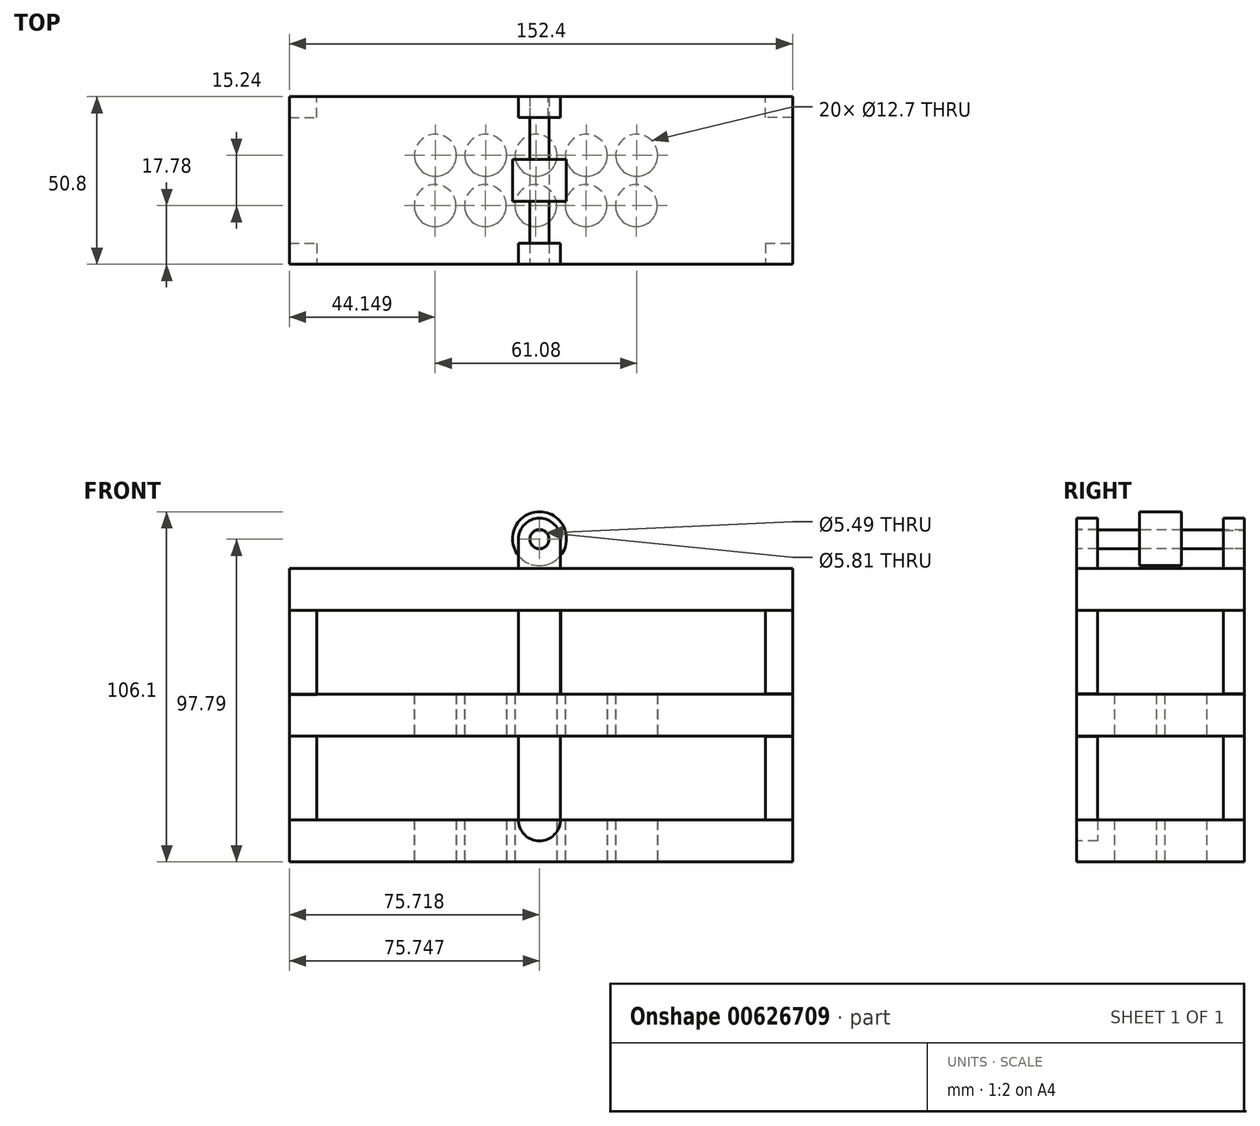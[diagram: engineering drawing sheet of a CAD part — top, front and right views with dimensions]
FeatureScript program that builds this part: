
annotation { "Feature Type Name" : "Feature", "Feature Type Description" : "" }
export const myFeature = defineFeature(function(context is Context, id is Id, definition is map)
    precondition{}
    {
        {
            var Q0;
            Q0=qCreatedBy(makeId("Front.planeOp"),FACE);
            var sketch = newSketch(context, id + "F0", { "sketchPlane" : qUnion([Q0])});
            skLineSegment(sketch, "E0", {"start": v(0, 88.9) * mm, "end": v(152.4, 88.9) * mm});
            skLineSegment(sketch, "E1", {"start": v(152.4, 0) * mm, "end": v(0, 0) * mm});
            skLineSegment(sketch, "E2", {"start": v(0, 0) * mm, "end": v(0, 12.7) * mm});
            skLineSegment(sketch, "E3", {"start": v(0, 12.7) * mm, "end": v(152.4, 12.7) * mm});
            skLineSegment(sketch, "E4", {"start": v(152.4, 12.7) * mm, "end": v(152.4, 0) * mm});
            skLineSegment(sketch, "E5", {"start": v(0, 38.1) * mm, "end": v(152.4, 38.1) * mm});
            skLineSegment(sketch, "E6", {"start": v(152.4, 38.1) * mm, "end": v(152.4, 50.8) * mm});
            skLineSegment(sketch, "E7", {"start": v(152.4, 50.8) * mm, "end": v(0, 50.8) * mm});
            skLineSegment(sketch, "E8", {"start": v(0, 50.8) * mm, "end": v(0, 38.1) * mm});
            skLineSegment(sketch, "E9", {"start": v(152.4, 88.9) * mm, "end": v(152.4, 76.2) * mm});
            skLineSegment(sketch, "E10", {"start": v(152.4, 76.2) * mm, "end": v(0, 76.2) * mm});
            skLineSegment(sketch, "E11", {"start": v(0, 76.2) * mm, "end": v(0, 88.9) * mm});
            skSolve(sketch);
        }
        {
            var Q0;
            Q0=makeQuery(id+"F0.imprint","IMPRINT",FACE,{"disambiguationData":[TD([[makeQuery(id+"F0.imprint","IMPRINT",EDGE,{"derivedFrom":sQuery(id+"F0.wireOp",EDGE,"E0")}),-1.0]])]});
            var Q1;
            Q1=makeQuery(id+"F0.imprint","IMPRINT",FACE,{"disambiguationData":[TD([[makeQuery(id+"F0.imprint","IMPRINT",EDGE,{"derivedFrom":sQuery(id+"F0.wireOp",EDGE,"E5")}),1.0]])]});
            var Q2;
            Q2=makeQuery(id+"F0.imprint","IMPRINT",FACE,{"disambiguationData":[TD([[makeQuery(id+"F0.imprint","IMPRINT",EDGE,{"derivedFrom":sQuery(id+"F0.wireOp",EDGE,"E1")}),-1.0]])]});
            extrude(context, id + "F1", {"entities" : qUnion([Q0, Q1, Q2]), "oppositeDirection" : true, "depth" : 50.8 * mm, "offsetDistance" : 25.4 * mm});
        }
        {
            var Q0;
            Q0=qCreatedBy(makeId("Front.planeOp"),FACE);
            var sketch = newSketch(context, id + "F2", { "sketchPlane" : qUnion([Q0])});
            skLineSegment(sketch, "E12", {"start": v(0, 12.76) * mm, "end": v(8.26, 12.76) * mm});
            skLineSegment(sketch, "E13", {"start": v(8.26, 12.76) * mm, "end": v(8.26, 38.1) * mm});
            skLineSegment(sketch, "E14", {"start": v(8.26, 38.1) * mm, "end": v(0, 38.1) * mm});
            skLineSegment(sketch, "E15", {"start": v(0, 38.1) * mm, "end": v(0, 12.76) * mm});
            skLineSegment(sketch, "E16", {"start": v(8.26, 50.75) * mm, "end": v(0, 50.75) * mm});
            skLineSegment(sketch, "E17", {"start": v(0, 50.75) * mm, "end": v(0, 76.24) * mm});
            skLineSegment(sketch, "E18", {"start": v(0, 76.24) * mm, "end": v(8.26, 76.24) * mm});
            skLineSegment(sketch, "E19", {"start": v(8.26, 76.24) * mm, "end": v(8.26, 50.75) * mm});
            skSolve(sketch);
        }
        {
            var Q0;
            Q0=makeQuery(id+"F1.opExtrude","CAP_FACE",FACE,{"disambiguationData":[OSD([sQuery(id+"F0.wireOp",EDGE,"E1"),sQuery(id+"F0.wireOp",EDGE,"E2"),sQuery(id+"F0.wireOp",EDGE,"E3"),sQuery(id+"F0.wireOp",EDGE,"E4")])],"isStart":true});
            var sketch = newSketch(context, id + "F3", { "sketchPlane" : qUnion([Q0])});
            skLineSegment(sketch, "E20", {"start": v(152.4, 12.7) * mm, "end": v(152.4, 37.95) * mm});
            skLineSegment(sketch, "E21", {"start": v(152.4, 37.95) * mm, "end": v(144.14, 37.95) * mm});
            skLineSegment(sketch, "E22", {"start": v(144.14, 37.95) * mm, "end": v(144.14, 12.7) * mm});
            skLineSegment(sketch, "E23", {"start": v(144.14, 12.7) * mm, "end": v(152.4, 12.7) * mm});
            skLineSegment(sketch, "E24", {"start": v(152.4, 50.88) * mm, "end": v(152.4, 76.21) * mm});
            skLineSegment(sketch, "E25", {"start": v(152.4, 76.21) * mm, "end": v(144.14, 76.21) * mm});
            skLineSegment(sketch, "E26", {"start": v(144.14, 76.21) * mm, "end": v(144.14, 50.88) * mm});
            skLineSegment(sketch, "E27", {"start": v(144.14, 50.88) * mm, "end": v(152.4, 50.88) * mm});
            skSolve(sketch);
        }
        {
            var Q0;
            Q0=makeQuery(id+"F3.imprint","IMPRINT",FACE,{"disambiguationData":[TD([[makeQuery(id+"F3.imprint","IMPRINT",EDGE,{"derivedFrom":sQuery(id+"F3.wireOp",EDGE,"E24")}),1.0]])]});
            var Q1;
            Q1=makeQuery(id+"F3.imprint","IMPRINT",FACE,{"disambiguationData":[TD([[makeQuery(id+"F3.imprint","IMPRINT",EDGE,{"derivedFrom":sQuery(id+"F3.wireOp",EDGE,"E20")}),1.0]])]});
            var Q2;
            Q2=makeQuery(id+"F2.imprint","IMPRINT",FACE,{"disambiguationData":[TD([[makeQuery(id+"F2.imprint","IMPRINT",EDGE,{"derivedFrom":sQuery(id+"F2.wireOp",EDGE,"E12")}),1.0]])]});
            var Q3;
            Q3=makeQuery(id+"F2.imprint","IMPRINT",FACE,{"disambiguationData":[TD([[makeQuery(id+"F2.imprint","IMPRINT",EDGE,{"derivedFrom":sQuery(id+"F2.wireOp",EDGE,"E16")}),-1.0]])]});
            extrude(context, id + "F4", {"entities" : qUnion([Q0, Q1, Q2, Q3]), "oppositeDirection" : true, "depth" : 6.35 * mm, "offsetDistance" : 25.4 * mm});
        }
        {
            var Q0;
            Q0=makeQuery(id+"F1.opExtrude","CAP_FACE",FACE,{"disambiguationData":[OSD([sQuery(id+"F0.wireOp",EDGE,"E1"),sQuery(id+"F0.wireOp",EDGE,"E2"),sQuery(id+"F0.wireOp",EDGE,"E3"),sQuery(id+"F0.wireOp",EDGE,"E4")])],"isStart":false});
            var sketch = newSketch(context, id + "F5", { "sketchPlane" : qUnion([Q0])});
            skLineSegment(sketch, "E28", {"start": v(-152.4, 12.7) * mm, "end": v(-152.4, 38.13) * mm});
            skLineSegment(sketch, "E29", {"start": v(-152.4, 38.13) * mm, "end": v(-144.14, 38.13) * mm});
            skLineSegment(sketch, "E30", {"start": v(-144.14, 38.13) * mm, "end": v(-144.14, 12.7) * mm});
            skLineSegment(sketch, "E31", {"start": v(-144.14, 12.7) * mm, "end": v(-152.4, 12.7) * mm});
            skLineSegment(sketch, "E32", {"start": v(-152.4, 50.94) * mm, "end": v(-144.14, 50.94) * mm});
            skLineSegment(sketch, "E33", {"start": v(-144.14, 50.94) * mm, "end": v(-144.14, 76.26) * mm});
            skLineSegment(sketch, "E34", {"start": v(-144.14, 76.26) * mm, "end": v(-152.4, 76.26) * mm});
            skLineSegment(sketch, "E35", {"start": v(-152.4, 76.26) * mm, "end": v(-152.4, 50.94) * mm});
            skLineSegment(sketch, "E36", {"start": v(0, 12.7) * mm, "end": v(0, 38.13) * mm});
            skLineSegment(sketch, "E37", {"start": v(0, 38.13) * mm, "end": v(-8.26, 38.13) * mm});
            skLineSegment(sketch, "E38", {"start": v(-8.26, 38.13) * mm, "end": v(-8.26, 12.7) * mm});
            skLineSegment(sketch, "E39", {"start": v(-8.26, 12.7) * mm, "end": v(0, 12.7) * mm});
            skSolve(sketch);
        }
        {
            var Q0;
            Q0=makeQuery(id+"F1.opExtrude","CAP_FACE",FACE,{"disambiguationData":[OSD([sQuery(id+"F0.wireOp",EDGE,"E5"),sQuery(id+"F0.wireOp",EDGE,"E6"),sQuery(id+"F0.wireOp",EDGE,"E7"),sQuery(id+"F0.wireOp",EDGE,"E8")])],"isStart":false});
            var sketch = newSketch(context, id + "F6", { "sketchPlane" : qUnion([Q0])});
            skLineSegment(sketch, "E40", {"start": v(0, 50.8) * mm, "end": v(0, 76.22) * mm});
            skLineSegment(sketch, "E41", {"start": v(0, 76.22) * mm, "end": v(-8.26, 76.22) * mm});
            skLineSegment(sketch, "E42", {"start": v(-8.26, 76.22) * mm, "end": v(-8.25, 50.8) * mm});
            skLineSegment(sketch, "E43", {"start": v(-8.25, 50.8) * mm, "end": v(0, 50.8) * mm});
            skSolve(sketch);
        }
        {
            var Q0;
            Q0=makeQuery(id+"F5.imprint","IMPRINT",FACE,{"disambiguationData":[TD([[makeQuery(id+"F5.imprint","IMPRINT",EDGE,{"derivedFrom":sQuery(id+"F5.wireOp",EDGE,"E32")}),1.0]])]});
            var Q1;
            Q1=makeQuery(id+"F5.imprint","IMPRINT",FACE,{"disambiguationData":[TD([[makeQuery(id+"F5.imprint","IMPRINT",EDGE,{"derivedFrom":sQuery(id+"F5.wireOp",EDGE,"E28")}),-1.0]])]});
            var Q2;
            Q2=makeQuery(id+"F5.imprint","IMPRINT",FACE,{"disambiguationData":[TD([[makeQuery(id+"F5.imprint","IMPRINT",EDGE,{"derivedFrom":sQuery(id+"F5.wireOp",EDGE,"E36")}),1.0]])]});
            var Q3;
            Q3=makeQuery(id+"F6.imprint","IMPRINT",FACE,{"disambiguationData":[TD([[makeQuery(id+"F6.imprint","IMPRINT",EDGE,{"derivedFrom":sQuery(id+"F6.wireOp",EDGE,"E40")}),1.0]])]});
            extrude(context, id + "F7", {"entities" : qUnion([Q0, Q1, Q2, Q3]), "oppositeDirection" : true, "depth" : 6.35 * mm, "offsetDistance" : 25.4 * mm});
        }
        {
            var Q0;
            Q0=makeQuery(id+"F1.opExtrude","CAP_FACE",FACE,{"disambiguationData":[OSD([sQuery(id+"F0.wireOp",EDGE,"E5"),sQuery(id+"F0.wireOp",EDGE,"E6"),sQuery(id+"F0.wireOp",EDGE,"E7"),sQuery(id+"F0.wireOp",EDGE,"E8")])],"isStart":true});
            var sketch = newSketch(context, id + "F8", { "sketchPlane" : qUnion([Q0])});
            skLineSegment(sketch, "E44", {"start": v(69.38, 38.1) * mm, "end": v(82.08, 38.1) * mm});
            skSolve(sketch);
        }
        {
            var Q0;
            Q0=makeQuery(id+"F1.opExtrude","CAP_FACE",FACE,{"disambiguationData":[OSD([sQuery(id+"F0.wireOp",EDGE,"E1"),sQuery(id+"F0.wireOp",EDGE,"E2"),sQuery(id+"F0.wireOp",EDGE,"E3"),sQuery(id+"F0.wireOp",EDGE,"E4")])],"isStart":true});
            var sketch = newSketch(context, id + "F9", { "sketchPlane" : qUnion([Q0])});
            skLineSegment(sketch, "E45", {"start": v(69.4, 12.7) * mm, "end": v(82.1, 12.7) * mm});
            skLineSegment(sketch, "E46", {"start": v(69.4, 12.7) * mm, "end": v(69.4, 38.1) * mm});
            skLineSegment(sketch, "E47", {"start": v(69.4, 88.9) * mm, "end": v(82.1, 88.9) * mm});
            skLineSegment(sketch, "E48", {"start": v(82.1, 76.2) * mm, "end": v(82.1, 50.8) * mm});
            skLineSegment(sketch, "E49", {"start": v(69.4, 88.9) * mm, "end": v(69.4, 97.8) * mm});
            skLineSegment(sketch, "E50", {"start": v(82.1, 88.9) * mm, "end": v(82.1, 97.8) * mm});
            skArc(sketch, "E51", {"start": v(82.1, 97.8) * mm, "mid": v(75.75, 104.14) * mm, "end": v(69.4, 97.8) * mm});
            skArc(sketch, "E52", {"start": v(69.4, 12.7) * mm, "mid": v(75.75, 6.35) * mm, "end": v(82.1, 12.7) * mm});
            skCircle(sketch, "E53", {"center": v(75.75, 97.8) * mm, "radius": 2.9 * mm});
            skPoint(sketch, "E54.startSnap0", {"position": v(69.4, 50.8) * mm});
            skPoint(sketch, "E54.endSnap0", {"position": v(69.4, 50.8) * mm});
            skLineSegment(sketch, "E55.trimOffspring", {"start": v(69.4, 50.8) * mm, "end": v(69.4, 76.2) * mm});
            skLineSegment(sketch, "E56.trimOffspring", {"start": v(82.1, 38.1) * mm, "end": v(82.1, 12.7) * mm});
            skLineSegment(sketch, "E57", {"start": v(69.4, 50.8) * mm, "end": v(82.1, 50.8) * mm});
            skLineSegment(sketch, "E58", {"start": v(69.4, 38.1) * mm, "end": v(82.1, 38.1) * mm});
            skLineSegment(sketch, "E59", {"start": v(69.4, 76.2) * mm, "end": v(82.1, 76.2) * mm});
            skPoint(sketch, "E60.orphan", {"position": v(67.93, 88.9) * mm});
            skSolve(sketch);
        }
        {
            var Q0;
            Q0=makeQuery(id+"F9.imprint","IMPRINT",FACE,{"disambiguationData":[TD([[makeQuery(id+"F9.imprint","IMPRINT",EDGE,{"derivedFrom":sQuery(id+"F9.wireOp",EDGE,"E49")}),-1.0]])]});
            var Q1;
            Q1=makeQuery(id+"F9.imprint","IMPRINT",FACE,{"disambiguationData":[TD([[makeQuery(id+"F9.imprint","IMPRINT",EDGE,{"derivedFrom":sQuery(id+"F9.wireOp",EDGE,"E48")}),-1.0]])]});
            var Q2;
            Q2=makeQuery(id+"F9.imprint","IMPRINT",FACE,{"disambiguationData":[TD([[makeQuery(id+"F9.imprint","IMPRINT",EDGE,{"derivedFrom":sQuery(id+"F9.wireOp",EDGE,"E45")}),1.0]])]});
            var Q3;
            Q3=makeQuery(id+"F9.imprint","IMPRINT",FACE,{"disambiguationData":[TD([[makeQuery(id+"F9.imprint","IMPRINT",EDGE,{"derivedFrom":sQuery(id+"F9.wireOp",EDGE,"E45")}),-1.0]])]});
            extrude(context, id + "F10", {"entities" : qUnion([Q0, Q1, Q2, Q3]), "oppositeDirection" : true, "depth" : 6.35 * mm, "offsetDistance" : 25.4 * mm});
        }
        {
            var Q0;
            Q0=makeQuery(id+"F1.opExtrude","CAP_FACE",FACE,{"disambiguationData":[OSD([sQuery(id+"F0.wireOp",EDGE,"E1"),sQuery(id+"F0.wireOp",EDGE,"E2"),sQuery(id+"F0.wireOp",EDGE,"E3"),sQuery(id+"F0.wireOp",EDGE,"E4")])],"isStart":false});
            var sketch = newSketch(context, id + "F11", { "sketchPlane" : qUnion([Q0])});
            skLineSegment(sketch, "E61", {"start": v(-82.03, 12.7) * mm, "end": v(-82.03, 38.1) * mm});
            skLineSegment(sketch, "E62", {"start": v(-82.03, 38.1) * mm, "end": v(-69.33, 38.1) * mm});
            skLineSegment(sketch, "E63", {"start": v(-69.33, 38.1) * mm, "end": v(-69.33, 12.7) * mm});
            skLineSegment(sketch, "E64", {"start": v(-69.33, 12.7) * mm, "end": v(-82.03, 12.7) * mm});
            skSolve(sketch);
        }
        {
            var Q0;
            Q0=makeQuery(id+"F1.opExtrude","CAP_FACE",FACE,{"disambiguationData":[OSD([sQuery(id+"F0.wireOp",EDGE,"E5"),sQuery(id+"F0.wireOp",EDGE,"E6"),sQuery(id+"F0.wireOp",EDGE,"E7"),sQuery(id+"F0.wireOp",EDGE,"E8")])],"isStart":false});
            var sketch = newSketch(context, id + "F12", { "sketchPlane" : qUnion([Q0])});
            skLineSegment(sketch, "E65", {"start": v(-82.18, 50.8) * mm, "end": v(-82.18, 76.2) * mm});
            skLineSegment(sketch, "E66", {"start": v(-82.18, 76.2) * mm, "end": v(-69.48, 76.2) * mm});
            skLineSegment(sketch, "E67", {"start": v(-69.48, 76.2) * mm, "end": v(-69.48, 50.8) * mm});
            skLineSegment(sketch, "E68", {"start": v(-69.48, 50.8) * mm, "end": v(-82.18, 50.8) * mm});
            skSolve(sketch);
        }
        {
            var Q0;
            Q0=makeQuery(id+"F1.opExtrude","CAP_FACE",FACE,{"disambiguationData":[OSD([sQuery(id+"F0.wireOp",EDGE,"E0"),sQuery(id+"F0.wireOp",EDGE,"E9"),sQuery(id+"F0.wireOp",EDGE,"E10"),sQuery(id+"F0.wireOp",EDGE,"E11")])],"isStart":false});
            var sketch = newSketch(context, id + "F13", { "sketchPlane" : qUnion([Q0])});
            skLineSegment(sketch, "E69", {"start": v(-82.06, 88.9) * mm, "end": v(-82.06, 97.8) * mm});
            skLineSegment(sketch, "E70", {"start": v(-69.38, 88.9) * mm, "end": v(-69.38, 97.8) * mm});
            skArc(sketch, "E71", {"start": v(-69.38, 97.8) * mm, "mid": v(-75.72, 104.13) * mm, "end": v(-82.06, 97.8) * mm});
            skCircle(sketch, "E72", {"center": v(-75.72, 97.8) * mm, "radius": 2.74 * mm});
            skSolve(sketch);
        }
        {
            var Q0;
            Q0=makeQuery(id+"F11.imprint","IMPRINT",FACE,{"disambiguationData":[TD([[makeQuery(id+"F11.imprint","IMPRINT",EDGE,{"derivedFrom":sQuery(id+"F11.wireOp",EDGE,"E61")}),-1.0]])]});
            var Q1;
            Q1=makeQuery(id+"F12.imprint","IMPRINT",FACE,{"disambiguationData":[TD([[makeQuery(id+"F12.imprint","IMPRINT",EDGE,{"derivedFrom":sQuery(id+"F12.wireOp",EDGE,"E65")}),-1.0]])]});
            var Q2;
            {var subQ1=sQuery(id+"F13.wireOp",EDGE,"E69");Q2=makeQuery(id+"F13.imprint","IMPRINT",FACE,{"disambiguationData":[TD([[makeQuery(id+"F13.imprint","IMPRINT",EDGE,{"derivedFrom":subQ1}),-1.0]])]});}
            extrude(context, id + "F14", {"entities" : qUnion([Q0, Q1, Q2]), "oppositeDirection" : true, "depth" : 6.35 * mm, "offsetDistance" : 25.4 * mm});
        }
        {
            var Q0;
            Q0=makeQuery(id+"F10.opExtrude","CAP_FACE",FACE,{"disambiguationData":[OSD([sQuery(id+"F9.wireOp",EDGE,"E49"),sQuery(id+"F9.wireOp",EDGE,"E50"),sQuery(id+"F9.wireOp",EDGE,"E51"),sQuery(id+"F9.wireOp",EDGE,"E53"),sQuery(id+"F9.wireOp",EDGE,"E47")])],"isStart":true});
            var sketch = newSketch(context, id + "F15", { "sketchPlane" : qUnion([Q0])});
            skCircle(sketch, "E73", {"center": v(75.75, 97.8) * mm, "radius": 2.87 * mm});
            skSolve(sketch);
        }
        {
            var Q0;
            Q0=makeQuery(id+"F15.imprint","IMPRINT",FACE,{"disambiguationData":[TD([[makeQuery(id+"F15.imprint","IMPRINT",EDGE,{"derivedFrom":sQuery(id+"F15.wireOp",EDGE,"E73")}),1.0]])]});
            extrude(context, id + "F16", {"entities" : qUnion([Q0]), "oppositeDirection" : true, "depth" : 50.8 * mm, "offsetDistance" : 25.4 * mm});
        }
        {
            var Q0;
            Q0=qCreatedBy(makeId("Front.planeOp"),FACE);
            cPlane(context, id + "F17", {"entities" : qUnion([Q0]), "cplaneType" : CPlaneType.OFFSET, "offset" : 25.4 * mm, "oppositeDirection" : true, "width" : 152.4 * mm, "height" : 152.4 * mm});
        }
        {
            var Q0;
            Q0=qCreatedBy(id+"F17.planeOp",FACE);
            var sketch = newSketch(context, id + "F18", { "sketchPlane" : qUnion([Q0])});
            skCircle(sketch, "E74", {"center": v(75.76, 97.94) * mm, "radius": 8.17 * mm});
            skSolve(sketch);
        }
        {
            var Q0;
            Q0=makeQuery(id+"F18.imprint","IMPRINT",FACE,{"disambiguationData":[TD([[makeQuery(id+"F18.imprint","IMPRINT",EDGE,{"derivedFrom":sQuery(id+"F18.wireOp",EDGE,"E74")}),1.0]])]});
            extrude(context, id + "F19", {"entities" : qUnion([Q0]), "depth" : 6.35 * mm, "offsetDistance" : 25.4 * mm, "hasSecondDirection" : true, "secondDirectionOppositeDirection" : true, "secondDirectionDepth" : 6.35 * mm});
        }
        {
            var Q0;
            Q0=makeQuery(id+"F1.opExtrude","SWEPT_FACE",FACE,{"disambiguationData":[OSD([sQuery(id+"F0.wireOp",EDGE,"E1")])]});
            var sketch = newSketch(context, id + "F20", { "sketchPlane" : qUnion([Q0])});
            skCircle(sketch, "E75", {"center": v(59.39, -17.78) * mm, "radius": 6.35 * mm});
            skCircle(sketch, "E76", {"center": v(74.63, -17.78) * mm, "radius": 6.35 * mm});
            skCircle(sketch, "E77", {"center": v(89.87, -17.78) * mm, "radius": 6.35 * mm});
            skCircle(sketch, "E78", {"center": v(44.15, -17.78) * mm, "radius": 6.35 * mm});
            skCircle(sketch, "E79", {"center": v(44.27, -33.02) * mm, "radius": 6.35 * mm});
            skCircle(sketch, "E80", {"center": v(105.1, -17.78) * mm, "radius": 6.35 * mm});
            skCircle(sketch, "E81", {"center": v(74.75, -33.02) * mm, "radius": 6.35 * mm});
            skCircle(sketch, "E82", {"center": v(89.99, -33.02) * mm, "radius": 6.35 * mm});
            skCircle(sketch, "E83", {"center": v(105.23, -33.02) * mm, "radius": 6.35 * mm});
            skCircle(sketch, "E84", {"center": v(59.5, -33.02) * mm, "radius": 6.35 * mm});
            skSolve(sketch);
        }
        {
            var Q0;
            Q0 = qSketchRegion(id + "F20", true);
            extrude(context, id + "F21", {"entities" : qUnion([Q0]), "operationType" : NewBodyOperationType.REMOVE, "oppositeDirection" : true, "depth" : 52.83 * mm, "offsetDistance" : 25.4 * mm});
        }
    });
